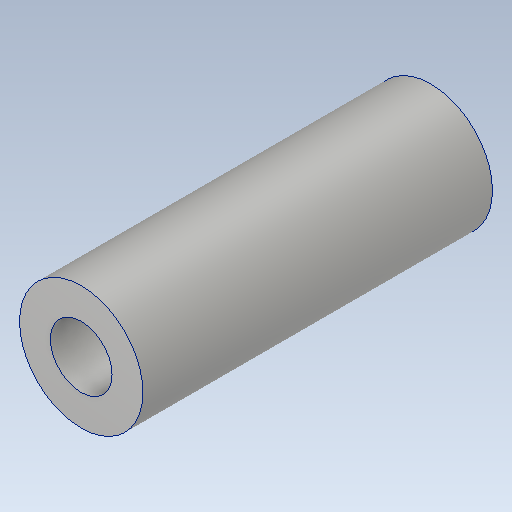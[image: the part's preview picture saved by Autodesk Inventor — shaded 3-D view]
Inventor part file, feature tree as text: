
AUTODESK INVENTOR PART (.ipt)
format: ipt  version: 2020.2 (Build 242310000, 310)  size: 111,104 bytes
history: native  units: mm
features: other x2, extrude x2, sketch x2, projected_geometry x1
ambient origin geometry x8: Origin, YZ Plane, XZ Plane, XY Plane, X Axis, Y Axis, Z Axis, Center Point
bodies: Body1 (feature_tree)
feature tree (7):
  other  "ソリッド1"
  extrude  "押し出し1"  Depth=6.0mm
  other  "作業平面1"
  extrude  "押し出し2"  Depth=3.0mm
  sketch  "スケッチ1"
  sketch  "スケッチ2"
  projected_geometry  "投影ループ1"
